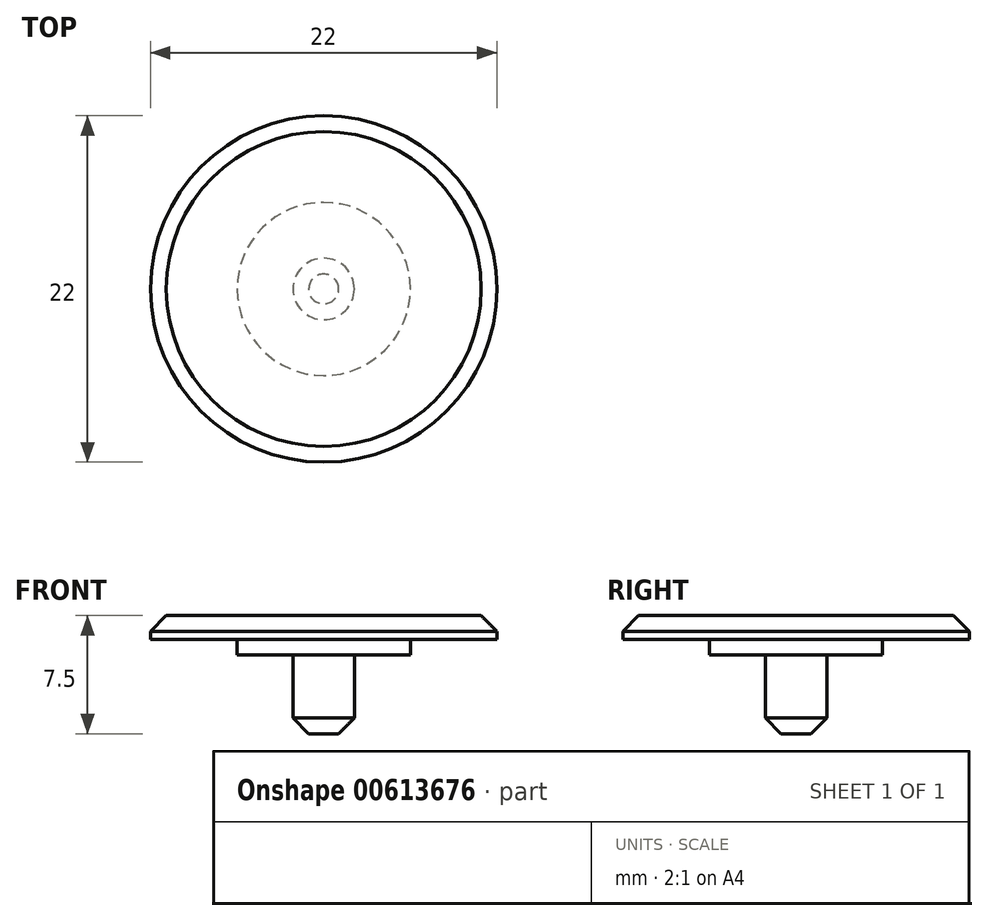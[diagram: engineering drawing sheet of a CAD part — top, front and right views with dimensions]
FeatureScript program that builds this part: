
annotation { "Feature Type Name" : "Feature", "Feature Type Description" : "" }
export const myFeature = defineFeature(function(context is Context, id is Id, definition is map)
    precondition{}
    {
        {
            var Q0;
            Q0=qCreatedBy(makeId("Top.planeOp"),FACE);
            var sketch = newSketch(context, id + "F0", { "sketchPlane" : qUnion([Q0])});
            skCircle(sketch, "E0", {"center": v(0, 0) * mm, "radius": 1.95 * mm});
            skSolve(sketch);
        }
        {
            var Q0;
            Q0=makeQuery(id+"F0.imprint","IMPRINT",FACE,{"disambiguationData":[TD([[makeQuery(id+"F0.imprint","IMPRINT",EDGE,{"derivedFrom":sQuery(id+"F0.wireOp",EDGE,"E0")}),1.0]])]});
            extrude(context, id + "F1", {"entities" : qUnion([Q0]), "depth" : 5 * mm, "offsetDistance" : 25 * mm});
        }
        {
            var Q0;
            Q0=makeQuery(id+"F1.opExtrude","CAP_FACE",FACE,{"disambiguationData":[OSD([sQuery(id+"F0.wireOp",EDGE,"E0")])],"isStart":false});
            var sketch = newSketch(context, id + "F2", { "sketchPlane" : qUnion([Q0])});
            skCircle(sketch, "E1", {"center": v(0, 0) * mm, "radius": 5.5 * mm});
            skSolve(sketch);
        }
        {
            var Q0;
            Q0=makeQuery(id+"F2.imprint","IMPRINT",FACE,{"disambiguationData":[TD([[makeQuery(id+"F2.imprint","IMPRINT",EDGE,{"derivedFrom":sQuery(id+"F2.wireOp",EDGE,"E1")}),1.0]])]});
            var Q1;
            Q1=makeQuery(id+"F2.imprint","IMPRINT",FACE,{"disambiguationData":[TD([[makeQuery(id+"F2.imprint","IMPRINT",EDGE,{"derivedFrom":makeQuery(id+"F1.opExtrude","CAP_EDGE",EDGE,{"disambiguationData":[OSD([sQuery(id+"F0.wireOp",EDGE,"E0")])],"isStart":false})}),1.0]])]});
            extrude(context, id + "F3", {"entities" : qUnion([Q0, Q1]), "operationType" : NewBodyOperationType.ADD, "depth" : 1 * mm, "offsetDistance" : 25 * mm});
        }
        {
            var Q0;
            Q0=makeQuery(id+"F3.opExtrude","CAP_FACE",FACE,{"disambiguationData":[OSD([sQuery(id+"F2.wireOp",EDGE,"E1")])],"isStart":false});
            var sketch = newSketch(context, id + "F4", { "sketchPlane" : qUnion([Q0])});
            skCircle(sketch, "E2", {"center": v(0, 0) * mm, "radius": 11 * mm});
            skSolve(sketch);
        }
        {
            var Q0;
            Q0=qSketchRegion(id+"F4",true);
            extrude(context, id + "F5", {"entities" : qUnion([Q0]), "operationType" : NewBodyOperationType.ADD, "depth" : 1.5 * mm, "offsetDistance" : 25 * mm});
        }
        {
            var Q0;
            Q0=makeQuery(id+"F5.opExtrude","CAP_EDGE",EDGE,{"disambiguationData":[OSD([sQuery(id+"F4.wireOp",EDGE,"E2")])],"isStart":false});
            var Q1;
            Q1=makeQuery(id+"F1.opExtrude","CAP_EDGE",EDGE,{"disambiguationData":[OSD([sQuery(id+"F0.wireOp",EDGE,"E0")])],"isStart":true});
            chamfer(context, id + "F6", {"entities" : qUnion([Q0, Q1]), "width" : 1 * mm, "tangentPropagation" : true});
        }
    });
